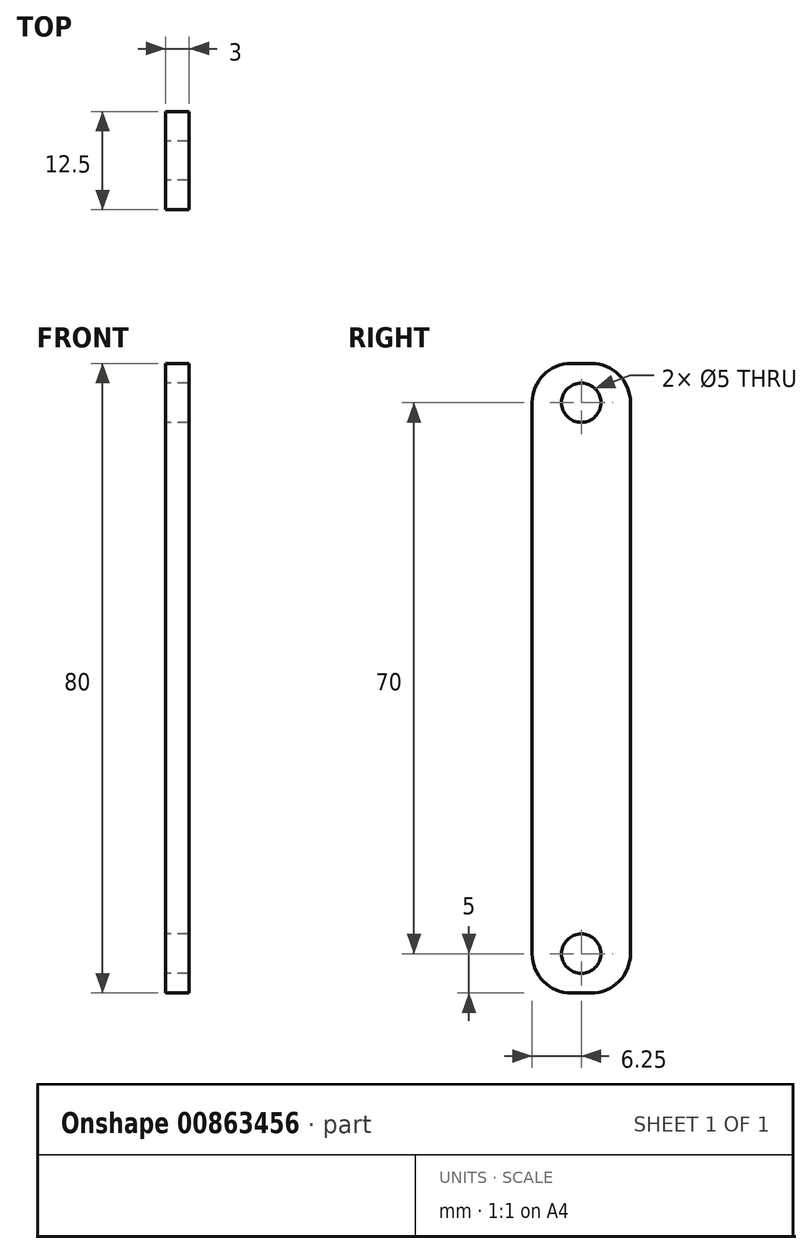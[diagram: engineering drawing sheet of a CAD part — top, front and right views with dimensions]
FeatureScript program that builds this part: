
annotation { "Feature Type Name" : "Feature", "Feature Type Description" : "" }
export const myFeature = defineFeature(function(context is Context, id is Id, definition is map)
    precondition{}
    {
        {
            var Q0;
            Q0=qCreatedBy(makeId("Top.planeOp"),FACE);
            var sketch = newSketch(context, id + "F0", { "sketchPlane" : qUnion([Q0])});
            skLineSegment(sketch, "E0.bottom", {"start": v(1.5, -6.25) * mm, "end": v(-1.5, -6.25) * mm});
            skLineSegment(sketch, "E0.top", {"start": v(1.5, 6.25) * mm, "end": v(-1.5, 6.25) * mm});
            skLineSegment(sketch, "E0.left", {"start": v(1.5, -6.25) * mm, "end": v(1.5, 6.25) * mm});
            skLineSegment(sketch, "E0.right", {"start": v(-1.5, -6.25) * mm, "end": v(-1.5, 6.25) * mm});
            skPoint(sketch, "E0.middle", {"position": v(0, 0) * mm});
            skSolve(sketch);
        }
        {
            var Q0;
            Q0=makeQuery(id+"F0.imprint","IMPRINT",FACE,{"disambiguationData":[TD([[makeQuery(id+"F0.imprint","IMPRINT",EDGE,{"derivedFrom":sQuery(id+"F0.wireOp",EDGE,"E0.bottom")}),-1.0]])]});
            extrude(context, id + "F1", {"entities" : qUnion([Q0]), "depth" : 80 * mm, "offsetDistance" : 25 * mm});
        }
        {
            var Q0;
            Q0=makeQuery(id+"F1.opExtrude","SWEPT_FACE",FACE,{"disambiguationData":[OSD([sQuery(id+"F0.wireOp",EDGE,"E0.right")])]});
            var sketch = newSketch(context, id + "F2", { "sketchPlane" : qUnion([Q0])});
            skCircle(sketch, "E1", {"center": v(0, 75) * mm, "radius": 2.5 * mm});
            skPoint(sketch, "E1.centerSnap0", {"position": v(0, 80) * mm});
            skCircle(sketch, "E2", {"center": v(0, 5) * mm, "radius": 2.5 * mm});
            skSolve(sketch);
        }
        {
            var Q0;
            Q0=sQuery(id+"F2.wireOp",VERTEX,"E1.center");
            var Q1;
            Q1=sQuery(id+"F2.wireOp",VERTEX,"E2.center");
            var Q2;
            Q2=makeQuery(id+"F1.opExtrude","SWEPT_BODY",BODY,{"disambiguationData":[OSD([sQuery(id+"F0.wireOp",EDGE,"E0.bottom"),sQuery(id+"F0.wireOp",EDGE,"E0.top"),sQuery(id+"F0.wireOp",EDGE,"E0.left"),sQuery(id+"F0.wireOp",EDGE,"E0.right")])]});
            hole(context, id + "F3", {"style" : HoleStyle.SIMPLE, "endStyle" : HoleEndStyle.THROUGH, "holeDiameter" : 5 * mm, "majorDiameter" : 5 * mm, "isTappedThrough" : true, "tappedDepth" : 12 * mm, "tapClearance" : 3, "locations" : qUnion([Q0, Q1]), "scope" : qUnion([Q2])});
        }
        {
            var Q0;
            Q0=makeQuery(id+"F1.opExtrude","CAP_EDGE",EDGE,{"disambiguationData":[OSD([sQuery(id+"F0.wireOp",EDGE,"E0.bottom")])],"isStart":false});
            var Q1;
            Q1=makeQuery(id+"F1.opExtrude","CAP_EDGE",EDGE,{"disambiguationData":[OSD([sQuery(id+"F0.wireOp",EDGE,"E0.top")])],"isStart":false});
            var Q2;
            Q2=makeQuery(id+"F1.opExtrude","CAP_EDGE",EDGE,{"disambiguationData":[OSD([sQuery(id+"F0.wireOp",EDGE,"E0.top")])],"isStart":true});
            var Q3;
            Q3=makeQuery(id+"F1.opExtrude","CAP_EDGE",EDGE,{"disambiguationData":[OSD([sQuery(id+"F0.wireOp",EDGE,"E0.bottom")])],"isStart":true});
            fillet(context, id + "F4", {"entities" : qUnion([Q0, Q1, Q2, Q3]), "radius" : 5 * mm, "tangentPropagation" : true, "allowEdgeOverflow" : false});
        }
    });
